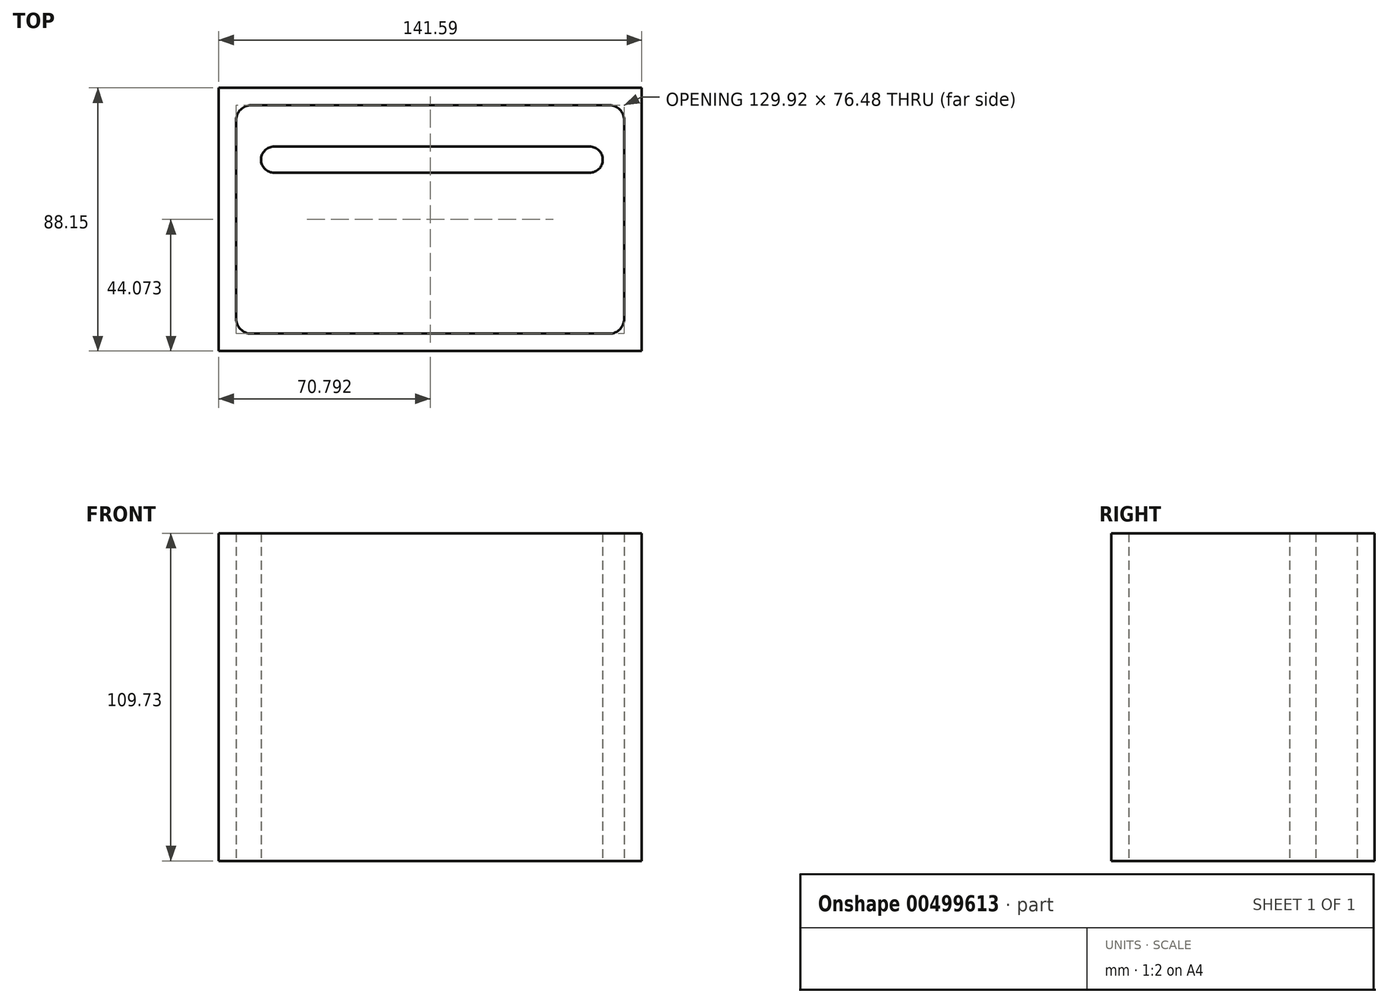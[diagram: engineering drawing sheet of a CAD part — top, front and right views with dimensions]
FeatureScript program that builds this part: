
annotation { "Feature Type Name" : "Feature", "Feature Type Description" : "" }
export const myFeature = defineFeature(function(context is Context, id is Id, definition is map)
    precondition{}
    {
        {
            var Q0;
            Q0=qCreatedBy(makeId("Top.planeOp"),FACE);
            var sketch = newSketch(context, id + "F0", { "sketchPlane" : qUnion([Q0])});
            skLineSegment(sketch, "E0.bottom", {"start": v(-56.43, 31.48) * mm, "end": v(63.5, 31.48) * mm});
            skLineSegment(sketch, "E0.top", {"start": v(-56.43, -45) * mm, "end": v(63.5, -45) * mm});
            skLineSegment(sketch, "E0.left", {"start": v(-61.43, 26.48) * mm, "end": v(-61.43, -40) * mm});
            skLineSegment(sketch, "E0.right", {"start": v(68.5, 26.48) * mm, "end": v(68.5, -40) * mm});
            skLineSegment(sketch, "E1.0", {"start": v(-67.26, 37.32) * mm, "end": v(74.33, 37.32) * mm});
            skLineSegment(sketch, "E1.1", {"start": v(-67.26, 37.32) * mm, "end": v(-67.26, -50.83) * mm});
            skLineSegment(sketch, "E1.2", {"start": v(-67.26, -50.83) * mm, "end": v(74.33, -50.83) * mm});
            skLineSegment(sketch, "E1.3", {"start": v(74.33, 37.32) * mm, "end": v(74.33, -50.83) * mm});
            skLineSegment(sketch, "E2", {"start": v(-48.73, 17.65) * mm, "end": v(56.9, 17.65) * mm});
            skLineSegment(sketch, "E3", {"start": v(56.9, 8.87) * mm, "end": v(-48.73, 8.87) * mm});
            skArc(sketch, "E4", {"start": v(56.9, 17.65) * mm, "mid": v(61.29, 13.26) * mm, "end": v(56.9, 8.87) * mm});
            skArc(sketch, "E5", {"start": v(-48.73, 17.65) * mm, "mid": v(-53.12, 13.26) * mm, "end": v(-48.73, 8.87) * mm});
            skCircle(sketch, "E6", {"center": v(-33.15, -21.44) * mm, "radius": 19.43 * mm});
            skEllipse(sketch, "E7", {"center": v(38.14, -17.84) * mm, "majorRadius": 31.83 * mm, "minorRadius": 11.26 * mm, "majorAxis": v(0.66, -0.75)});
            skCircle(sketch, "E8.cCircle", {"center": v(-33.15, -21.44) * mm, "radius": 19.43 * mm, "construction": true});
            skLineSegment(sketch, "E8.0", {"start": v(-14.18, -25.66) * mm, "end": v(-27.32, -39.98) * mm});
            skLineSegment(sketch, "E8.1", {"start": v(-27.32, -39.98) * mm, "end": v(-46.28, -35.76) * mm});
            skLineSegment(sketch, "E8.2", {"start": v(-46.28, -35.76) * mm, "end": v(-52.11, -17.22) * mm});
            skLineSegment(sketch, "E8.3", {"start": v(-52.11, -17.22) * mm, "end": v(-38.98, -2.9) * mm});
            skLineSegment(sketch, "E8.4", {"start": v(-38.98, -2.9) * mm, "end": v(-20.01, -7.13) * mm});
            skLineSegment(sketch, "E8.5", {"start": v(-20.01, -7.13) * mm, "end": v(-14.18, -25.66) * mm});
            skFitSpline(sketch, "E9", {"points": [v(-11.71, -8.01) * mm, v(3.53, -10.86) * mm, v(6.56, -19.67) * mm, v(7.18, -24.86) * mm, v(9.21, -30.23) * mm, v(21.1, -36.43) * mm, v(33.5, -37.2) * mm, v(20.83, -22.74) * mm], "startDerivative": vector(92.88, 7.35) * mm, "endDerivative": vector(-94.86, 85.78) * mm});
            skPoint(sketch, "E10.visualSharp", {"position": v(68.5, 31.48) * mm});
            skArc(sketch, "E10.filletArc", {"start": v(68.5, 26.48) * mm, "mid": v(67.03, 30.02) * mm, "end": v(63.5, 31.48) * mm});
            skPoint(sketch, "E11.visualSharp", {"position": v(68.5, -45) * mm});
            skArc(sketch, "E11.filletArc", {"start": v(63.5, -45) * mm, "mid": v(67.03, -43.53) * mm, "end": v(68.5, -40) * mm});
            skPoint(sketch, "E12.visualSharp", {"position": v(-61.43, -45) * mm});
            skArc(sketch, "E12.filletArc", {"start": v(-61.43, -40) * mm, "mid": v(-59.96, -43.53) * mm, "end": v(-56.43, -45) * mm});
            skPoint(sketch, "E13.visualSharp", {"position": v(-61.43, 31.48) * mm});
            skArc(sketch, "E13.filletArc", {"start": v(-56.43, 31.48) * mm, "mid": v(-59.96, 30.02) * mm, "end": v(-61.43, 26.48) * mm});
            skSolve(sketch);
        }
        {
            var Q0;
            Q0=makeQuery(id+"F0.imprint","IMPRINT",FACE,{"disambiguationData":[TD([[makeQuery(id+"F0.imprint","IMPRINT",EDGE,{"derivedFrom":sQuery(id+"F0.wireOp",EDGE,"E2")}),-1.0]])]});
            var Q1;
            Q1=makeQuery(id+"F0.imprint","IMPRINT",FACE,{"disambiguationData":[TD([[makeQuery(id+"F0.imprint","IMPRINT",EDGE,{"derivedFrom":sQuery(id+"F0.wireOp",EDGE,"E0.bottom")}),1.0]])]});
            extrude(context, id + "F1", {"entities" : qUnion([Q0, Q1]), "depth" : 109.73 * mm});
        }
    });
